# Revit family: 0047782 Feilo Sylvania Lighting Fixture START PANEL 600 3000K DALI G4
name_source: partatom
category: Lighting Fixtures
revit_build: Autodesk Revit 2017 (Build: 20190507_1515(x64)
units: mm (PartAtom-declared; Revit-internal decimal feet)

## family parameters
Cut with Voids When Loaded = No
Host = Face
Light Source = Yes
OmniClass Number = 23.80.70.00
OmniClass Title = Lighting
Part Type = Normal
Room Calculation Point = No
Round Connector Dimension = Use Diameter
Shared = No

## types (1)
- 0047782 START PANEL 600 3000K DALI G4
    Apparent Load = 36 VA
    Assembly Code = D5020200
    AssetType = Fixed
    BezelOffset_FEILO = 30 mm  [stored 0.0984252 ft]
    ClassificationName = Uniclass2015
    ClassificationValue = EF_70_80
    Color Filter = 16777215
    Cost = 0 $
    Default Elevation = 1219 mm
    Description = LED back-lit recessed IP44 panel, 3000K Warm White, 4500lm delivered from 36W, 125lm/W total system effciency, energy efficient external DALI dimmable tridonic driver, even distribution of light throughout fixture, long lifetime of 50,000 hours (L70), size (HxWxD) 596x596x65mm.
    Dimming Lamp Color Temperature Shift = <None>
    DimmingControlOptions = Dimmable
    DocumentationLiterature = http://www.sylvania-lighting.com
    DurationUnit = hours
    ElectricShockClassification = Class II
    Emit Shape Visible in Rendering = No
    Emit from Rectangle Length = 566 mm
    Emit from Rectangle Width = 566 mm
    ExpectedLife = 50000
    IfcExportAs = IfcLightFixtureType
    IfcExportType = IfcLightFixtureType
    ImpactProtectionIndex = IK03
    IngressProtection = IP44
    InputNominalFrequency = 50/60 Hz
    InputVoltage = 220-240V~
    Keynote = 16500
    Lamp = LED
    LampColourRenderingIndex = 80
    LampColourTemperature = 3000 K
    LampMacAdamStep = 6
    LampNominalLuminous = 4500 lm
    LampsType = LED
    Length_FEILO = 596 mm  [stored 1.95538 ft]
    LuminousEfficacy = 120 lm/W
    Manufacturer = Feilo Sylvania
    ManufacturerName = Feilo Sylvania
    Material = steel housing
    Material_1_FEILO = Body-Sylvania-Start Panel LED DALI-White
    Material_2_FEILO = Diffuser-Sylvania-Start Panel LED DALI
    Material_3_FEILO = <By Category>
    Material_4_FEILO = <By Category>
    Model = START PANEL 600 3000K DALI G4
    ModelNumber = 0047782
    ModelReference = START PANEL 600 3000K DALI G4
    Name = START PANEL 600 3000K DALI G4
    NominalDepth = 596 mm  [stored 1.95538 ft]
    NominalHeight = 63 mm  [stored 0.206693 ft]
    NominalLength = 596 mm  [stored 1.95538 ft]
    Photometric Web File = 0047782.ies
    PowerConsumption = 36 W
    PowerFactor = 0.96
    Tilt Angle = -90.00°
    Type Image = <None>
    TypeName = START PANEL 600 3000K DALI G4
    URL = http://www.sylvania-lighting.com
    Voltage = 230 V
    Weight = 2.6 kg

note: [stored X ft] marks values corroborated as IEEE doubles in the binary element streams (Revit-internal decimal feet)

## geometry (parser evidence)
native form markers: Sweep x1
no freeform markers — native parametric forms only
